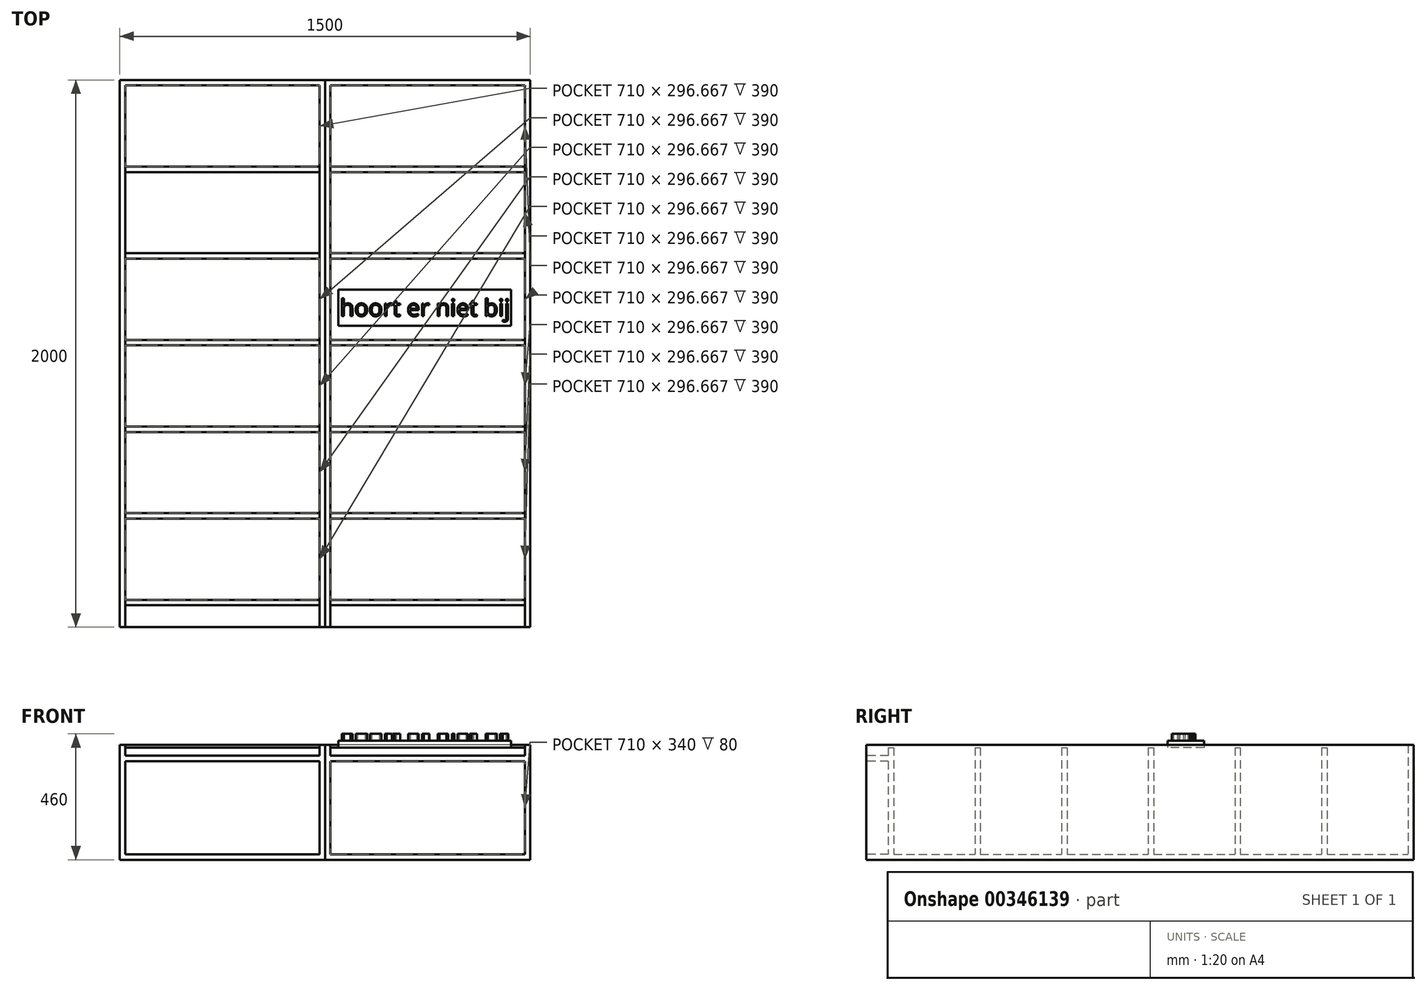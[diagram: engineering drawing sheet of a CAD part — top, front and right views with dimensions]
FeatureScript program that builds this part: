
annotation { "Feature Type Name" : "Feature", "Feature Type Description" : "" }
export const myFeature = defineFeature(function(context is Context, id is Id, definition is map)
    precondition{}
    {
        {
            var Q0;
            Q0=qCreatedBy(makeId("Top.planeOp"),FACE);
            var sketch = newSketch(context, id + "F0", { "sketchPlane" : qUnion([Q0])});
            skLineSegment(sketch, "E0.bottom", {"start": v(355, -990) * mm, "end": v(375, -990) * mm});
            skLineSegment(sketch, "E0.left", {"start": v(355, -990) * mm, "end": v(355, 990) * mm});
            skLineSegment(sketch, "E0.right", {"start": v(375, -990) * mm, "end": v(375, 1010) * mm});
            skLineSegment(sketch, "E1.bottom", {"start": v(375, 1010) * mm, "end": v(-375, 1010) * mm});
            skLineSegment(sketch, "E1.top", {"start": v(355, 990) * mm, "end": v(-355, 990) * mm});
            skLineSegment(sketch, "E2.top", {"start": v(-375, -990) * mm, "end": v(-355, -990) * mm});
            skLineSegment(sketch, "E2.left", {"start": v(-375, 1010) * mm, "end": v(-375, -990) * mm});
            skLineSegment(sketch, "E2.right", {"start": v(-355, 990) * mm, "end": v(-355, -990) * mm});
            skLineSegment(sketch, "E3", {"start": v(355, 990) * mm, "end": v(355, 1010) * mm, "construction": true});
            skLineSegment(sketch, "E4", {"start": v(-355, 990) * mm, "end": v(355, -990) * mm, "construction": true});
            skLineSegment(sketch, "E5", {"start": v(-355, -990) * mm, "end": v(355, 990) * mm, "construction": true});
            skPoint(sketch, "E6", {"position": v(0, 0) * mm});
            skLineSegment(sketch, "E7.bottom", {"start": v(-355, 693.33) * mm, "end": v(355, 693.33) * mm});
            skLineSegment(sketch, "E7.top", {"start": v(-355, 673.33) * mm, "end": v(355, 673.33) * mm});
            skLineSegment(sketch, "E7.left", {"start": v(-355, 693.33) * mm, "end": v(-355, 673.33) * mm});
            skLineSegment(sketch, "E7.right", {"start": v(355, 693.33) * mm, "end": v(355, 673.33) * mm});
            skLineSegment(sketch, "E8.bottom", {"start": v(-355, 376.67) * mm, "end": v(355, 376.67) * mm});
            skLineSegment(sketch, "E8.top", {"start": v(-355, 356.67) * mm, "end": v(355, 356.67) * mm});
            skLineSegment(sketch, "E8.left", {"start": v(-355, 376.67) * mm, "end": v(-355, 356.67) * mm});
            skLineSegment(sketch, "E8.right", {"start": v(355, 376.67) * mm, "end": v(355, 356.67) * mm});
            skLineSegment(sketch, "E9.bottom", {"start": v(-355, 60) * mm, "end": v(355, 60) * mm});
            skLineSegment(sketch, "E9.top", {"start": v(-355, 40) * mm, "end": v(355, 40) * mm});
            skLineSegment(sketch, "E9.left", {"start": v(-355, 60) * mm, "end": v(-355, 40) * mm});
            skLineSegment(sketch, "E9.right", {"start": v(355, 60) * mm, "end": v(355, 40) * mm});
            skLineSegment(sketch, "E10.bottom", {"start": v(-355, -276.67) * mm, "end": v(355, -276.67) * mm});
            skLineSegment(sketch, "E10.top", {"start": v(-355, -256.67) * mm, "end": v(355, -256.67) * mm});
            skLineSegment(sketch, "E10.left", {"start": v(-355, -256.67) * mm, "end": v(-355, -276.67) * mm});
            skLineSegment(sketch, "E10.right", {"start": v(355, -256.67) * mm, "end": v(355, -276.67) * mm});
            skLineSegment(sketch, "E11.bottom", {"start": v(-355, -573.33) * mm, "end": v(355, -573.33) * mm});
            skLineSegment(sketch, "E11.top", {"start": v(-355, -593.33) * mm, "end": v(355, -593.33) * mm});
            skLineSegment(sketch, "E11.left", {"start": v(-355, -573.33) * mm, "end": v(-355, -593.33) * mm});
            skLineSegment(sketch, "E11.right", {"start": v(355, -573.33) * mm, "end": v(355, -593.33) * mm});
            skLineSegment(sketch, "E12.bottom", {"start": v(-355, -890) * mm, "end": v(355, -890) * mm});
            skLineSegment(sketch, "E12.top", {"start": v(-355, -910) * mm, "end": v(355, -910) * mm});
            skLineSegment(sketch, "E12.left", {"start": v(-355, -890) * mm, "end": v(-355, -910) * mm});
            skLineSegment(sketch, "E12.right", {"start": v(355, -890) * mm, "end": v(355, -910) * mm});
            skLineSegment(sketch, "E13", {"start": v(355, 693.33) * mm, "end": v(355, 990) * mm, "construction": true});
            skLineSegment(sketch, "E14", {"start": v(355, 673.33) * mm, "end": v(355, 376.67) * mm, "construction": true});
            skLineSegment(sketch, "E15", {"start": v(355, 356.67) * mm, "end": v(355, 60) * mm, "construction": true});
            skLineSegment(sketch, "E16", {"start": v(355, 40) * mm, "end": v(355, -256.67) * mm, "construction": true});
            skLineSegment(sketch, "E17", {"start": v(355, -276.67) * mm, "end": v(355, -573.33) * mm, "construction": true});
            skLineSegment(sketch, "E18", {"start": v(355, -593.33) * mm, "end": v(355, -890) * mm, "construction": true});
            skSolve(sketch);
        }
        {
            var Q0;
            {var subQ25=sQuery(id+"F0.wireOp",EDGE,"E0.bottom");Q0=makeQuery(id+"F0.imprint","IMPRINT",FACE,{"disambiguationData":[TD([[makeQuery(id+"F0.imprint","IMPRINT",EDGE,{"derivedFrom":subQ25}),1.0]])]});}
            extrude(context, id + "F1", {"entities" : qUnion([Q0]), "depth" : 400 * mm});
        }
        {
            var Q0;
            {var subQ0=makeQuery(id+"F1.opExtrude","CAP_FACE",FACE,{"disambiguationData":[OSD([sQuery(id+"F0.wireOp",EDGE,"E0.bottom"),sQuery(id+"F0.wireOp",EDGE,"E0.left"),sQuery(id+"F0.wireOp",EDGE,"E0.right"),sQuery(id+"F0.wireOp",EDGE,"E1.bottom"),sQuery(id+"F0.wireOp",EDGE,"E1.top"),sQuery(id+"F0.wireOp",EDGE,"E2.top"),sQuery(id+"F0.wireOp",EDGE,"E2.left"),sQuery(id+"F0.wireOp",EDGE,"E2.right"),sQuery(id+"F0.wireOp",EDGE,"E7.left"),sQuery(id+"F0.wireOp",EDGE,"E7.right"),sQuery(id+"F0.wireOp",EDGE,"E8.left"),sQuery(id+"F0.wireOp",EDGE,"E8.right"),sQuery(id+"F0.wireOp",EDGE,"E9.left"),sQuery(id+"F0.wireOp",EDGE,"E9.right"),sQuery(id+"F0.wireOp",EDGE,"E10.left"),sQuery(id+"F0.wireOp",EDGE,"E10.right"),sQuery(id+"F0.wireOp",EDGE,"E11.left"),sQuery(id+"F0.wireOp",EDGE,"E11.right"),sQuery(id+"F0.wireOp",EDGE,"E12.left"),sQuery(id+"F0.wireOp",EDGE,"E12.right")])],"isStart":false});Q0=makeQuery(id+"F10.boolean.opBoolean","MERGE",FACE,{"derivedFrom":[subQ0,makeQuery(id+"F10.opPattern","COPY",FACE,{"derivedFrom":subQ0,"instanceName":"1"})]});}
            cPlane(context, id + "F2", {"entities" : qUnion([Q0]), "cplaneType" : CPlaneType.OFFSET, "offset" : 10 * mm, "oppositeDirection" : true, "width" : 150 * mm, "height" : 150 * mm});
        }
        {
            var Q0;
            Q0=qCreatedBy(id+"F2.planeOp",FACE);
            var sketch = newSketch(context, id + "F3", { "sketchPlane" : qUnion([Q0])});
            skLineSegment(sketch, "E19.bottom", {"start": v(-325.87, 244.13) * mm, "end": v(304.85, 244.13) * mm});
            skLineSegment(sketch, "E19.top", {"start": v(-325.87, 111.25) * mm, "end": v(304.85, 111.25) * mm});
            skLineSegment(sketch, "E19.left", {"start": v(-325.87, 244.13) * mm, "end": v(-325.87, 111.25) * mm});
            skLineSegment(sketch, "E19.right", {"start": v(304.85, 244.13) * mm, "end": v(304.85, 111.25) * mm});
            skSolve(sketch);
        }
        {
            var Q0;
            Q0 = qSketchRegion(id + "F3", true);
            extrude(context, id + "F4", {"entities" : qUnion([Q0]), "depth" : 25 * mm});
        }
        {
            var Q0;
            Q0=makeQuery(id+"F0.imprint","IMPRINT",FACE,{"disambiguationData":[TD([[makeQuery(id+"F0.imprint","IMPRINT",EDGE,{"derivedFrom":sQuery(id+"F0.wireOp",EDGE,"E7.bottom")}),-1.0]])]});
            var Q1;
            Q1=makeQuery(id+"F0.imprint","IMPRINT",FACE,{"disambiguationData":[TD([[makeQuery(id+"F0.imprint","IMPRINT",EDGE,{"derivedFrom":sQuery(id+"F0.wireOp",EDGE,"E8.bottom")}),-1.0]])]});
            var Q2;
            Q2=makeQuery(id+"F0.imprint","IMPRINT",FACE,{"disambiguationData":[TD([[makeQuery(id+"F0.imprint","IMPRINT",EDGE,{"derivedFrom":sQuery(id+"F0.wireOp",EDGE,"E9.bottom")}),-1.0]])]});
            var Q3;
            Q3=makeQuery(id+"F0.imprint","IMPRINT",FACE,{"disambiguationData":[TD([[makeQuery(id+"F0.imprint","IMPRINT",EDGE,{"derivedFrom":sQuery(id+"F0.wireOp",EDGE,"E10.bottom")}),1.0]])]});
            var Q4;
            Q4=makeQuery(id+"F0.imprint","IMPRINT",FACE,{"disambiguationData":[TD([[makeQuery(id+"F0.imprint","IMPRINT",EDGE,{"derivedFrom":sQuery(id+"F0.wireOp",EDGE,"E11.bottom")}),-1.0]])]});
            var Q5;
            Q5=makeQuery(id+"F0.imprint","IMPRINT",FACE,{"disambiguationData":[TD([[makeQuery(id+"F0.imprint","IMPRINT",EDGE,{"derivedFrom":sQuery(id+"F0.wireOp",EDGE,"E12.bottom")}),-1.0]])]});
            var Q6;
            Q6=makeQuery(id+"F4.opExtrude","CAP_FACE",FACE,{"disambiguationData":[OSD([sQuery(id+"F3.wireOp",EDGE,"E19.bottom"),sQuery(id+"F3.wireOp",EDGE,"E19.top"),sQuery(id+"F3.wireOp",EDGE,"E19.left"),sQuery(id+"F3.wireOp",EDGE,"E19.right")])],"isStart":true});
            extrude(context, id + "F5", {"entities" : qUnion([Q0, Q1, Q2, Q3, Q4, Q5]), "operationType" : NewBodyOperationType.ADD, "endBound" : BoundingType.UP_TO_SURFACE, "endBoundEntityFace" : qUnion([Q6]), "depth" : 390 * mm});
        }
        {
            var Q0;
            Q0=makeQuery(id+"F1.opExtrude","SWEPT_FACE",FACE,{"disambiguationData":[OSD([sQuery(id+"F0.wireOp",EDGE,"E2.top")])]});
            var sketch = newSketch(context, id + "F6", { "sketchPlane" : qUnion([Q0])});
            skLineSegment(sketch, "E20.0", {"start": v(355, 400) * mm, "end": v(375, 400) * mm});
            skLineSegment(sketch, "E21.bottom", {"start": v(-355, 360) * mm, "end": v(355, 360) * mm});
            skLineSegment(sketch, "E21.top", {"start": v(-355, 340) * mm, "end": v(355, 340) * mm});
            skLineSegment(sketch, "E21.left", {"start": v(-355, 360) * mm, "end": v(-355, 340) * mm});
            skLineSegment(sketch, "E21.right", {"start": v(355, 360) * mm, "end": v(355, 340) * mm});
            skLineSegment(sketch, "E22.0", {"start": v(-355, 390) * mm, "end": v(355, 390) * mm});
            skSolve(sketch);
        }
        {
            var Q0;
            Q0=makeQuery(id+"F6.imprint","IMPRINT",FACE,{"disambiguationData":[TD([[makeQuery(id+"F6.imprint","IMPRINT",EDGE,{"derivedFrom":sQuery(id+"F6.wireOp",EDGE,"E21.bottom")}),-1.0]])]});
            var Q1;
            Q1=makeQuery(id+"F5.opExtrude","SWEPT_FACE",FACE,{"disambiguationData":[OSD([sQuery(id+"F0.wireOp",EDGE,"E12.top")])]});
            extrude(context, id + "F7", {"entities" : qUnion([Q0]), "operationType" : NewBodyOperationType.ADD, "endBound" : BoundingType.UP_TO_SURFACE, "oppositeDirection" : true, "endBoundEntityFace" : qUnion([Q1]), "depth" : 25 * mm});
        }
        {
            var Q0;
            Q0=makeQuery(id+"F7.boolean.opBoolean","MERGE",FACE,{"derivedFrom":[makeQuery(id+"F1.opExtrude","SWEPT_FACE",FACE,{"disambiguationData":[OSD([sQuery(id+"F0.wireOp",EDGE,"E0.bottom")])]}),makeQuery(id+"F1.opExtrude","SWEPT_FACE",FACE,{"disambiguationData":[OSD([sQuery(id+"F0.wireOp",EDGE,"E2.top")])]}),makeQuery(id+"F7.opExtrude","CAP_FACE",FACE,{"disambiguationData":[OSD([sQuery(id+"F6.wireOp",EDGE,"E21.bottom"),sQuery(id+"F6.wireOp",EDGE,"E21.top"),sQuery(id+"F6.wireOp",EDGE,"E21.left"),sQuery(id+"F6.wireOp",EDGE,"E21.right")])],"isStart":true})]});
            var sketch = newSketch(context, id + "F8", { "sketchPlane" : qUnion([Q0])});
            skLineSegment(sketch, "E23.bottom", {"start": v(375, 0) * mm, "end": v(-375, 0) * mm});
            skLineSegment(sketch, "E23.top", {"start": v(375, -20) * mm, "end": v(-375, -20) * mm});
            skLineSegment(sketch, "E23.left", {"start": v(375, 0) * mm, "end": v(375, -20) * mm});
            skLineSegment(sketch, "E23.right", {"start": v(-375, 0) * mm, "end": v(-375, -20) * mm});
            skSolve(sketch);
        }
        {
            var Q0;
            Q0=makeQuery(id+"F8.imprint","IMPRINT",FACE,{"disambiguationData":[TD([[makeQuery(id+"F8.imprint","IMPRINT",EDGE,{"derivedFrom":sQuery(id+"F8.wireOp",EDGE,"E23.top")}),-1.0]])]});
            var Q1;
            Q1=makeQuery(id+"F1.opExtrude","SWEPT_FACE",FACE,{"disambiguationData":[OSD([sQuery(id+"F0.wireOp",EDGE,"E1.bottom")])]});
            extrude(context, id + "F9", {"entities" : qUnion([Q0]), "operationType" : NewBodyOperationType.ADD, "endBound" : BoundingType.UP_TO_SURFACE, "oppositeDirection" : true, "endBoundEntityFace" : qUnion([Q1]), "depth" : 25 * mm});
        }
        {
            var Q0;
            Q0=makeQuery(id+"F1.opExtrude","SWEPT_BODY",BODY,{"disambiguationData":[OSD([sQuery(id+"F0.wireOp",EDGE,"E0.bottom"),sQuery(id+"F0.wireOp",EDGE,"E0.left"),sQuery(id+"F0.wireOp",EDGE,"E0.right"),sQuery(id+"F0.wireOp",EDGE,"E1.bottom"),sQuery(id+"F0.wireOp",EDGE,"E1.top"),sQuery(id+"F0.wireOp",EDGE,"E2.top"),sQuery(id+"F0.wireOp",EDGE,"E2.left"),sQuery(id+"F0.wireOp",EDGE,"E2.right"),sQuery(id+"F0.wireOp",EDGE,"E7.left"),sQuery(id+"F0.wireOp",EDGE,"E7.right"),sQuery(id+"F0.wireOp",EDGE,"E8.left"),sQuery(id+"F0.wireOp",EDGE,"E8.right"),sQuery(id+"F0.wireOp",EDGE,"E9.left"),sQuery(id+"F0.wireOp",EDGE,"E9.right"),sQuery(id+"F0.wireOp",EDGE,"E10.left"),sQuery(id+"F0.wireOp",EDGE,"E10.right"),sQuery(id+"F0.wireOp",EDGE,"E11.left"),sQuery(id+"F0.wireOp",EDGE,"E11.right"),sQuery(id+"F0.wireOp",EDGE,"E12.left"),sQuery(id+"F0.wireOp",EDGE,"E12.right")])]});
            var Q1;
            Q1=makeQuery(id+"F9.boolean.opBoolean","MERGE",FACE,{"derivedFrom":[makeQuery(id+"F1.opExtrude","SWEPT_FACE",FACE,{"disambiguationData":[OSD([sQuery(id+"F0.wireOp",EDGE,"E2.left")])]}),makeQuery(id+"F9.opExtrude","SWEPT_FACE",FACE,{"disambiguationData":[OSD([sQuery(id+"F8.wireOp",EDGE,"E23.right")])]})]});
            mirror(context, id + "F10", {"entities" : qUnion([Q0]), "mirrorPlane" : qUnion([Q1])});
        }
        {
            var Q0;
            Q0=makeQuery(id+"F4.opExtrude","CAP_FACE",FACE,{"disambiguationData":[OSD([sQuery(id+"F3.wireOp",EDGE,"E19.bottom"),sQuery(id+"F3.wireOp",EDGE,"E19.top"),sQuery(id+"F3.wireOp",EDGE,"E19.left"),sQuery(id+"F3.wireOp",EDGE,"E19.right")])],"isStart":false});
            var sketch = newSketch(context, id + "F11", { "sketchPlane" : qUnion([Q0])});
            skText(sketch, "E24", { "text": "hoort er niet bij", "fontName": "OpenSans-Regular.ttf"});
            skLineSegment(sketch, "E25.0", {"start": v(304.85, 244.13) * mm, "end": v(304.85, 111.25) * mm});
            skLineSegment(sketch, "E26", {"start": v(304.85, 244.13) * mm, "end": v(304.85, 177.7) * mm, "construction": true});
            skLineSegment(sketch, "E27", {"start": v(299.85, 208.65) * mm, "end": v(299.85, 177.7) * mm, "construction": true});
            const initialGuessF11  = {"E24": [-0.32087, 0.14673, 1, 0, 0.06192]};
            skSetInitialGuess(sketch, initialGuessF11);
            skSolve(sketch);
        }
        {
            var Q0;
            Q0 = qSketchRegion(id + "F11", true);
            extrude(context, id + "F12", {"entities" : qUnion([Q0]), "operationType" : NewBodyOperationType.ADD, "depth" : 25 * mm});
        }
    });
